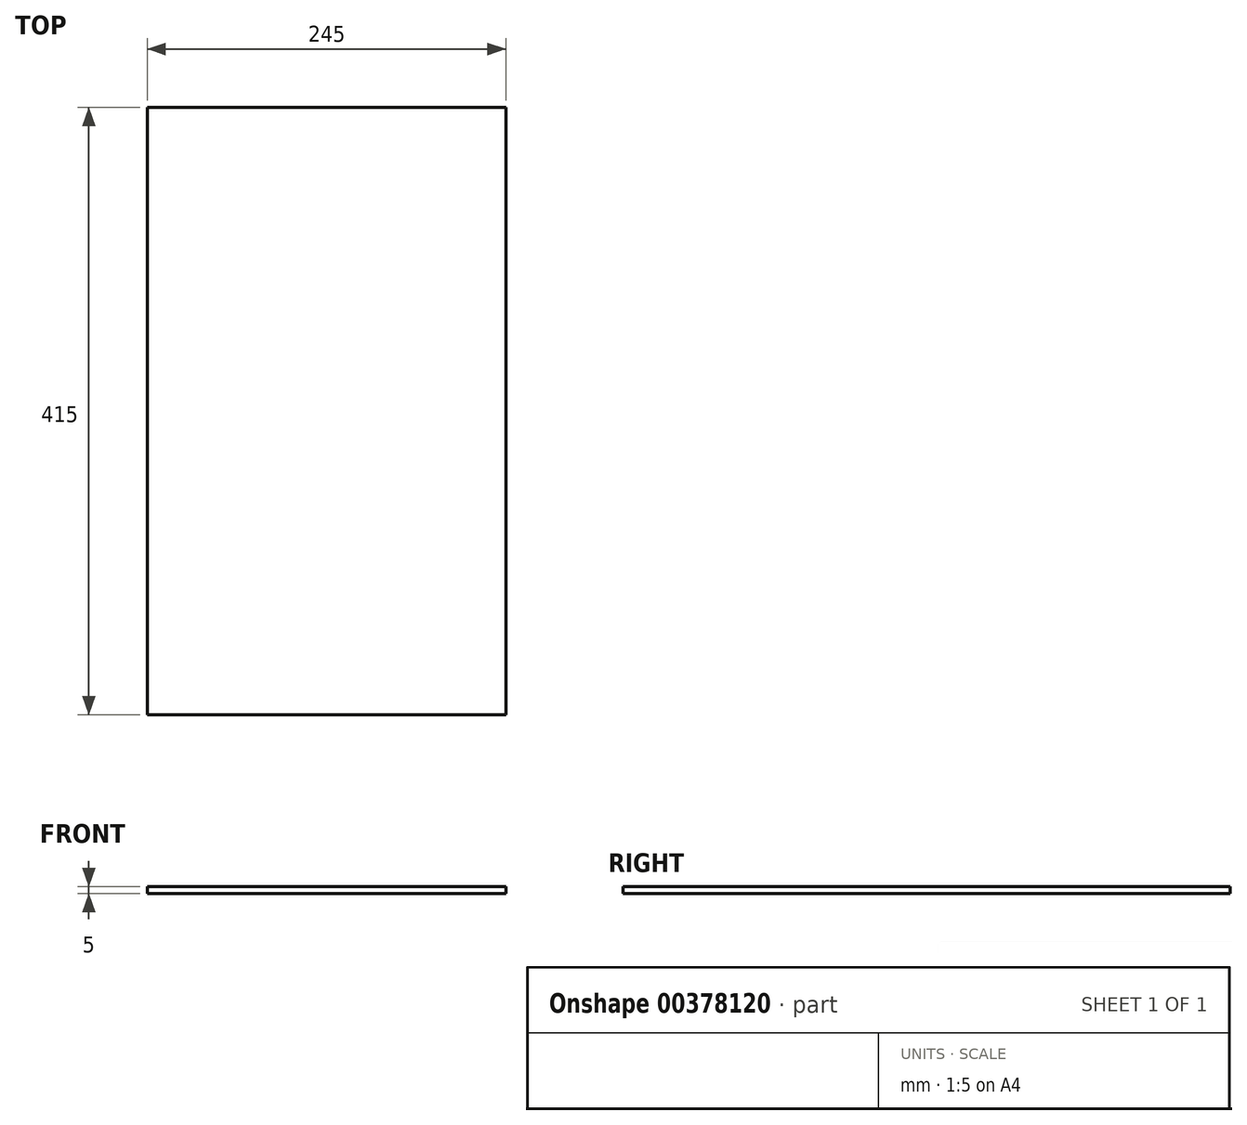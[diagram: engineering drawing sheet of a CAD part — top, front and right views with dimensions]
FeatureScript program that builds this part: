
annotation { "Feature Type Name" : "Feature", "Feature Type Description" : "" }
export const myFeature = defineFeature(function(context is Context, id is Id, definition is map)
    precondition{}
    {
        {
            var Q0;
            Q0=qCreatedBy(makeId("Top.planeOp"),FACE);
            var sketch = newSketch(context, id + "F0", { "sketchPlane" : qUnion([Q0])});
            skLineSegment(sketch, "E0.bottom", {"start": v(0, 0) * mm, "end": v(245, 0) * mm});
            skLineSegment(sketch, "E0.top", {"start": v(0, 415) * mm, "end": v(245, 415) * mm});
            skLineSegment(sketch, "E0.left", {"start": v(0, 0) * mm, "end": v(0, 415) * mm});
            skLineSegment(sketch, "E0.right", {"start": v(245, 0) * mm, "end": v(245, 415) * mm});
            skSolve(sketch);
        }
        {
            var Q0;
            Q0=makeQuery(id+"F0.imprint","IMPRINT",FACE,{"disambiguationData":[TD([[makeQuery(id+"F0.imprint","IMPRINT",EDGE,{"derivedFrom":sQuery(id+"F0.wireOp",EDGE,"E0.bottom")}),1.0]])]});
            extrude(context, id + "F1", {"entities" : qUnion([Q0]), "depth" : 5 * mm});
        }
    });
